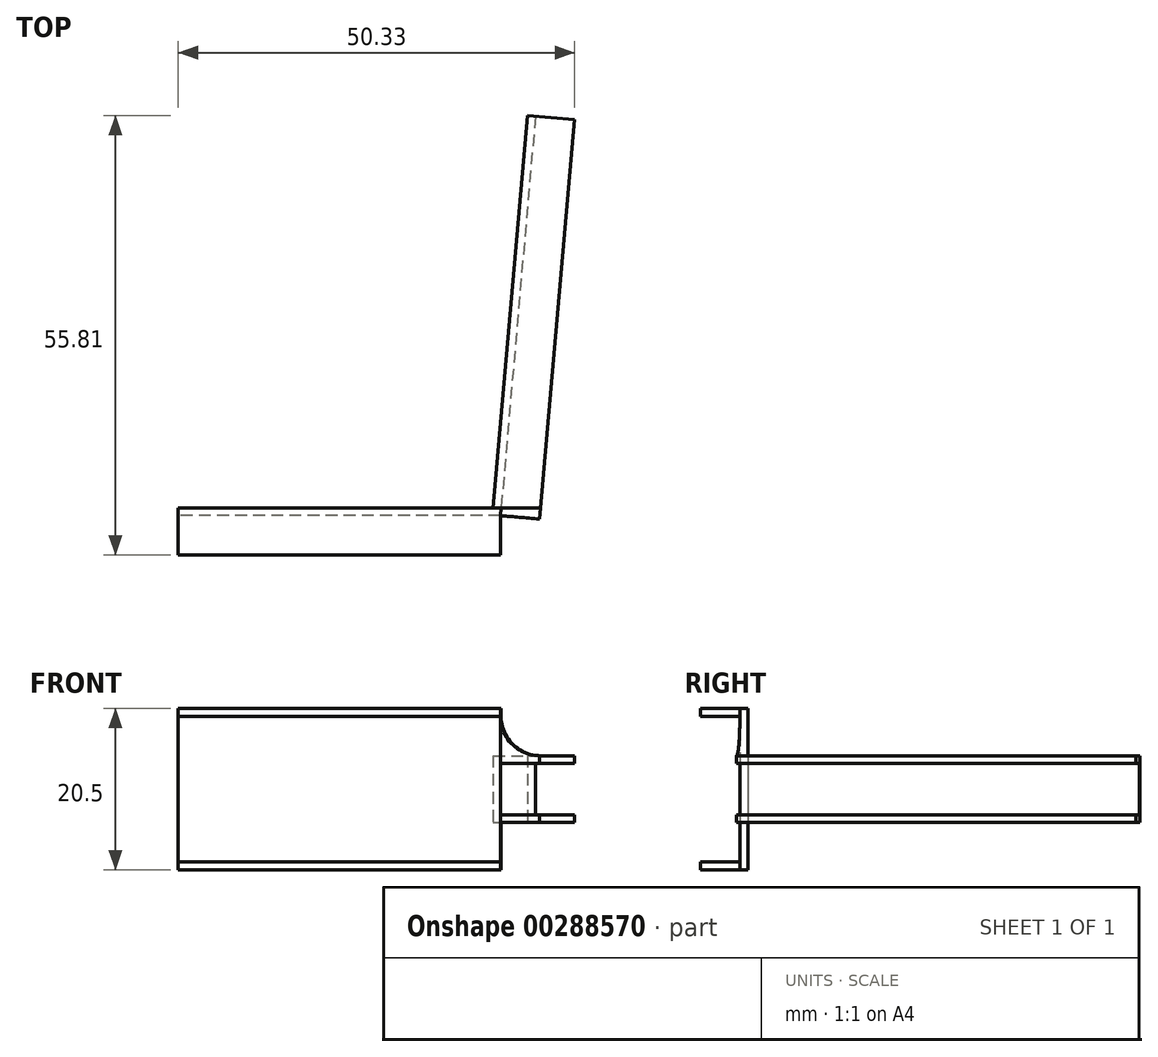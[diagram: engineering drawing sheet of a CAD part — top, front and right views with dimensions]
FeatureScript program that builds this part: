
annotation { "Feature Type Name" : "Feature", "Feature Type Description" : "" }
export const myFeature = defineFeature(function(context is Context, id is Id, definition is map)
    precondition{}
    {
        {
            var Q0;
            Q0=qCreatedBy(makeId("Top.planeOp"),FACE);
            var sketch = newSketch(context, id + "F0", { "sketchPlane" : qUnion([Q0])});
            skLineSegment(sketch, "E0", {"start": v(-40, 0) * mm, "end": v(0, 0) * mm});
            skLineSegment(sketch, "E1", {"start": v(0, 0) * mm, "end": v(4.36, 49.8) * mm});
            skLineSegment(sketch, "E2.0", {"start": v(0.92, -1) * mm, "end": v(5.35, 49.72) * mm});
            skLineSegment(sketch, "E2.1", {"start": v(-40, -1) * mm, "end": v(0.92, -1) * mm});
            skLineSegment(sketch, "E3", {"start": v(5.35, 49.72) * mm, "end": v(4.36, 49.8) * mm});
            skLineSegment(sketch, "E4", {"start": v(0, 0) * mm, "end": v(1, 0) * mm});
            skLineSegment(sketch, "E5", {"start": v(-40, 0) * mm, "end": v(-40, -1) * mm});
            skSolve(sketch);
        }
        {
            var Q0;
            Q0=makeQuery(id+"F0.imprint","IMPRINT",FACE,{"disambiguationData":[TD([[makeQuery(id+"F0.imprint","IMPRINT",EDGE,{"derivedFrom":sQuery(id+"F0.wireOp",EDGE,"E0")}),-1.0]])]});
            extrude(context, id + "F1", {"entities" : qUnion([Q0]), "endBound" : BoundingType.SYMMETRIC, "depth" : 20.5 * mm});
        }
        {
            var Q0;
            Q0=makeQuery(id+"F0.imprint","IMPRINT",FACE,{"disambiguationData":[TD([[makeQuery(id+"F0.imprint","IMPRINT",EDGE,{"derivedFrom":sQuery(id+"F0.wireOp",EDGE,"E1")}),-1.0]])]});
            extrude(context, id + "F2", {"entities" : qUnion([Q0]), "operationType" : NewBodyOperationType.ADD, "endBound" : BoundingType.SYMMETRIC, "depth" : 8.5 * mm});
        }
        {
            var Q0;
            {var subQ0=sQuery(id+"F0.wireOp",EDGE,"E2.0");Q0=makeQuery(id+"F2.boolean.opBoolean","MERGE",FACE,{"derivedFrom":[makeQuery(id+"F1.opExtrude","SWEPT_FACE",FACE,{"disambiguationData":[OSD([subQ0])]}),makeQuery(id+"F2.opExtrude","SWEPT_FACE",FACE,{"disambiguationData":[OSD([subQ0])]})]});}
            var sketch = newSketch(context, id + "F3", { "sketchPlane" : qUnion([Q0])});
            skLineSegment(sketch, "E6", {"start": v(50, -3.25) * mm, "end": v(-0.92, -3.25) * mm});
            skLineSegment(sketch, "E7", {"start": v(0.09, -4.25) * mm, "end": v(-0.92, -4.25) * mm});
            skLineSegment(sketch, "E8.MirrorCS", {"start": v(50, 3.25) * mm, "end": v(-0.92, 3.25) * mm});
            skLineSegment(sketch, "E9.MirrorCS", {"start": v(0.09, 4.25) * mm, "end": v(-0.92, 4.25) * mm});
            skSolve(sketch);
        }
        {
            var Q0;
            {var subQ0=sQuery(id+"F3.wireOp",EDGE,"E6");Q0=makeQuery(id+"F3.imprint","IMPRINT",FACE,{"disambiguationData":[TD([[makeQuery(id+"F3.imprint","IMPRINT",EDGE,{"derivedFrom":subQ0}),1.0]])]});}
            var Q1;
            {var subQ0=sQuery(id+"F3.wireOp",EDGE,"E8.MirrorCS");Q1=makeQuery(id+"F3.imprint","IMPRINT",FACE,{"disambiguationData":[TD([[makeQuery(id+"F3.imprint","IMPRINT",EDGE,{"derivedFrom":subQ0}),-1.0]])]});}
            extrude(context, id + "F4", {"entities" : qUnion([Q0, Q1]), "operationType" : NewBodyOperationType.ADD, "depth" : 5 * mm});
        }
        {
            var Q0;
            Q0=makeQuery(id+"F1.opExtrude","SWEPT_FACE",FACE,{"disambiguationData":[OSD([sQuery(id+"F0.wireOp",EDGE,"E2.1")])]});
            var sketch = newSketch(context, id + "F5", { "sketchPlane" : qUnion([Q0])});
            skLineSegment(sketch, "E10", {"start": v(1.83, -9.25) * mm, "end": v(-40, -9.25) * mm});
            skLineSegment(sketch, "E11.MirrorCS", {"start": v(1.83, 9.25) * mm, "end": v(-40, 9.25) * mm});
            skSolve(sketch);
        }
        {
            var Q0;
            {var subQ0=sQuery(id+"F5.wireOp",EDGE,"E11.MirrorCS");Q0=makeQuery(id+"F5.imprint","IMPRINT",FACE,{"disambiguationData":[TD([[makeQuery(id+"F5.imprint","IMPRINT",EDGE,{"derivedFrom":subQ0}),-1.0]])]});}
            var Q1;
            {var subQ0=sQuery(id+"F5.wireOp",EDGE,"E10");Q1=makeQuery(id+"F5.imprint","IMPRINT",FACE,{"disambiguationData":[TD([[makeQuery(id+"F5.imprint","IMPRINT",EDGE,{"derivedFrom":subQ0}),1.0]])]});}
            extrude(context, id + "F6", {"entities" : qUnion([Q0, Q1]), "operationType" : NewBodyOperationType.ADD, "depth" : 5 * mm});
        }
        {
            var Q0;
            Q0=makeQuery(id+"F4.opExtrude","CAP_EDGE",EDGE,{"disambiguationData":[OSD([sQuery(id+"F0.wireOp",EDGE,"E2.0"),sQuery(id+"F3.wireOp",EDGE,"E7")])],"isStart":true});
            var Q1;
            Q1=makeQuery(id+"F4.opExtrude","CAP_EDGE",EDGE,{"disambiguationData":[OSD([sQuery(id+"F0.wireOp",EDGE,"E2.0"),sQuery(id+"F3.wireOp",EDGE,"E9.MirrorCS")])],"isStart":true});
            var Q2;
            Q2=makeQuery(id+"F2.opExtrude","CAP_EDGE",EDGE,{"disambiguationData":[OSD([sQuery(id+"F0.wireOp",EDGE,"E4")])],"isStart":false});
            var Q3;
            Q3=makeQuery(id+"F2.opExtrude","CAP_EDGE",EDGE,{"disambiguationData":[OSD([sQuery(id+"F0.wireOp",EDGE,"E4")])],"isStart":true});
            var Q4;
            Q4=makeQuery(id+"F2.opExtrude","SWEPT_EDGE",EDGE,{"disambiguationData":[OSD([sQuery(id+"F0.wireOp",EDGE,"E0"),sQuery(id+"F0.wireOp",EDGE,"E1"),sQuery(id+"F0.wireOp",EDGE,"E4")])]});
            fillet(context, id + "F7", {"entities" : qUnion([Q0, Q1, Q2, Q3, Q4]), "radius" : 5 * mm, "tangentPropagation" : true, "allowEdgeOverflow" : false});
        }
    });
